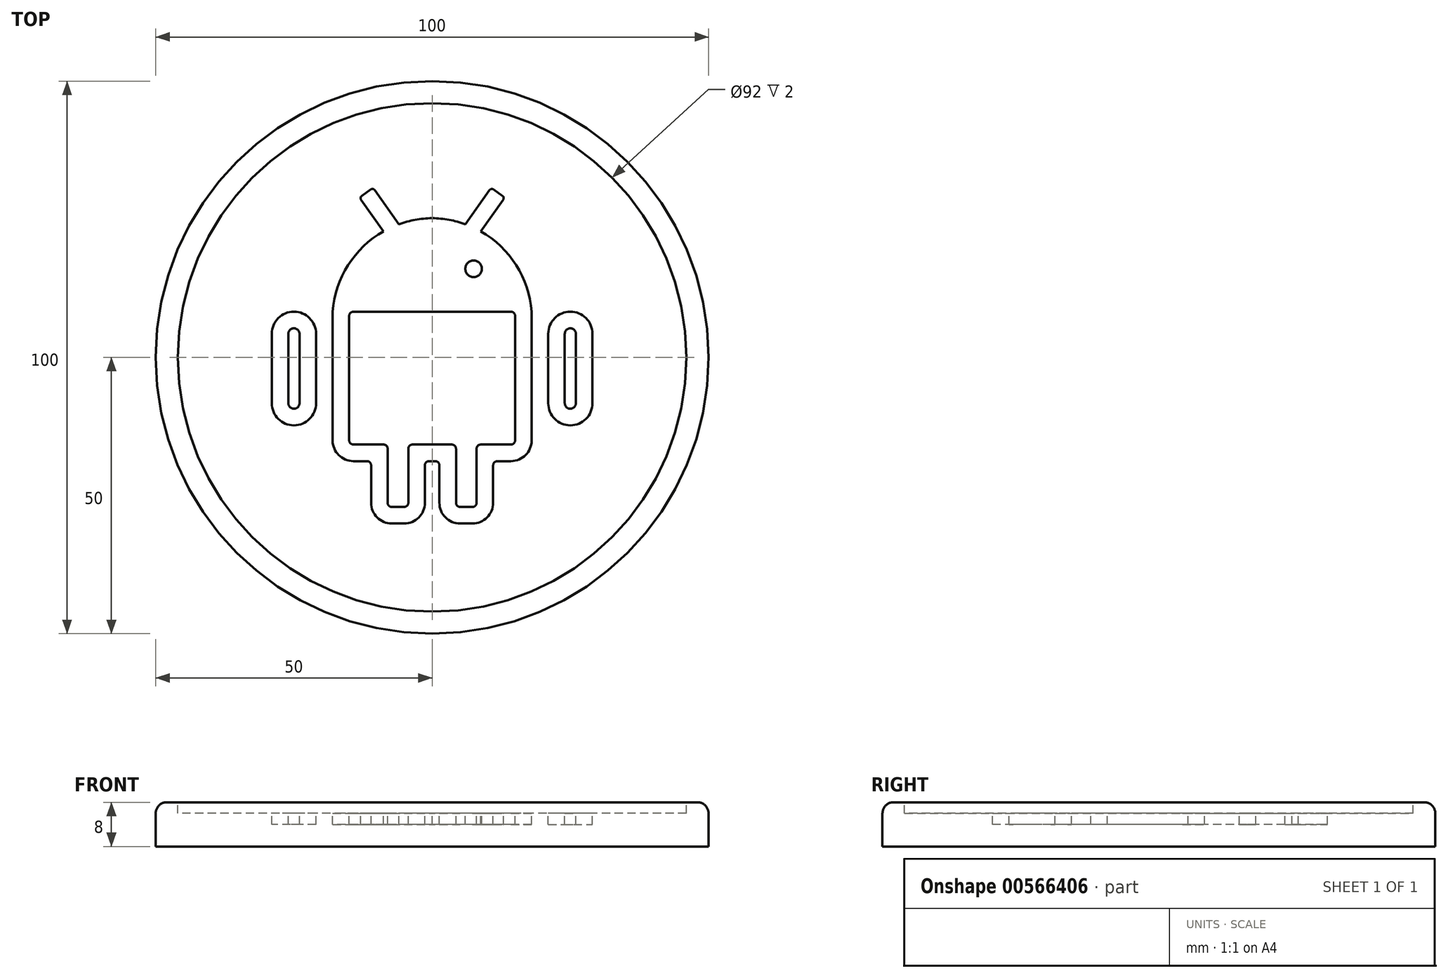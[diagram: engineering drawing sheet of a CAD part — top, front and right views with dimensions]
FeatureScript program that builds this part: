
annotation { "Feature Type Name" : "Feature", "Feature Type Description" : "" }
export const myFeature = defineFeature(function(context is Context, id is Id, definition is map)
    precondition{}
    {
        {
            var Q0;
            Q0=qCreatedBy(makeId("Top.planeOp"),FACE);
            var sketch = newSketch(context, id + "F0", { "sketchPlane" : qUnion([Q0])});
            skCircle(sketch, "E0", {"center": v(0, 0) * mm, "radius": 50 * mm});
            skSolve(sketch);
        }
        {
            assignVariable(context, id + "F1", {"name" : "Extrude", "anyValue" : 8 * mm});
        }
        {
            var Q0;
            Q0 = qSketchRegion(id + "F0", true);
            extrude(context, id + "F2", {"entities" : qUnion([Q0]), "depth" : getVariable(context, 'Extrude'), "offsetDistance" : 25 * mm});
        }
        {
            assignVariable(context, id + "F3", {"name" : "Fillet", "anyValue" : 2 * mm});
        }
        {
            var Q0;
            Q0=makeQuery(id+"F2.opExtrude","CAP_EDGE",EDGE,{"disambiguationData":[OSD([sQuery(id+"F0.wireOp",EDGE,"E0")])],"isStart":false});
            fillet(context, id + "F4", {"entities" : qUnion([Q0]), "radius" : getVariable(context, 'Fillet'), "tangentPropagation" : true, "allowEdgeOverflow" : false});
        }
        {
            assignVariable(context, id + "F5", {"name" : "Remove", "anyValue" : 2 * mm});
        }
        {
            var Q0;
            Q0=makeQuery(id+"F2.opExtrude","CAP_FACE",FACE,{"disambiguationData":[OSD([sQuery(id+"F0.wireOp",EDGE,"E0")])],"isStart":false});
            var sketch = newSketch(context, id + "F6", { "sketchPlane" : qUnion([Q0])});
            skCircle(sketch, "E1.0", {"center": v(0, 0) * mm, "radius": 48 * mm, "construction": true});
            skCircle(sketch, "E2", {"center": v(0, 0) * mm, "radius": 46 * mm});
            skSolve(sketch);
        }
        {
            var Q0;
            Q0 = qSketchRegion(id + "F6", true);
            extrude(context, id + "F7", {"entities" : qUnion([Q0]), "operationType" : NewBodyOperationType.REMOVE, "oppositeDirection" : true, "depth" : getVariable(context, 'Remove'), "offsetDistance" : 25 * mm});
        }
        {
            var Q0;
            Q0=makeQuery(id+"F7.boolean.opBoolean","COPY",FACE,{"derivedFrom":makeQuery(id+"F7.opExtrude","CAP_FACE",FACE,{"disambiguationData":[OSD([sQuery(id+"F6.wireOp",EDGE,"E2")])],"isStart":false})});
            var sketch = newSketch(context, id + "F8", { "sketchPlane" : qUnion([Q0])});
            skLineSegment(sketch, "E3", {"start": v(0, 48) * mm, "end": v(0, -48) * mm, "construction": true});
            skLineSegment(sketch, "E4", {"start": v(-26, 0) * mm, "end": v(48, 0) * mm, "construction": true});
            skLineSegment(sketch, "E5", {"start": v(-26, 30.77) * mm, "end": v(26, -30.77) * mm, "construction": true});
            skLineSegment(sketch, "E6", {"start": v(26, 30.77) * mm, "end": v(-26, -30.77) * mm, "construction": true});
            skPoint(sketch, "E7", {"position": v(0, 0) * mm});
            skLineSegment(sketch, "E8", {"start": v(0, 8.27) * mm, "end": v(-14.25, 8.27) * mm});
            skLineSegment(sketch, "E9", {"start": v(-15, 7.52) * mm, "end": v(-15, -15.02) * mm});
            skLineSegment(sketch, "E10", {"start": v(-14.25, -15.77) * mm, "end": v(-8.8, -15.77) * mm});
            skLineSegment(sketch, "E11", {"start": v(-8.04, -16.52) * mm, "end": v(-8.04, -26.32) * mm});
            skLineSegment(sketch, "E12", {"start": v(-7.3, -27.07) * mm, "end": v(-5.06, -27.07) * mm});
            skLineSegment(sketch, "E13", {"start": v(-4.31, -26.32) * mm, "end": v(-4.31, -16.52) * mm});
            skLineSegment(sketch, "E14", {"start": v(-3.56, -15.77) * mm, "end": v(0, -15.77) * mm});
            skLineSegment(sketch, "E15", {"start": v(0, 9.77) * mm, "end": v(-15, 9.77) * mm});
            skPoint(sketch, "E16.visualSharp", {"position": v(-15, 8.27) * mm});
            skArc(sketch, "E16.filletArc", {"start": v(-14.25, 8.27) * mm, "mid": v(-14.78, 8.05) * mm, "end": v(-15, 7.52) * mm});
            skPoint(sketch, "E17.visualSharp", {"position": v(-15, -15.77) * mm});
            skArc(sketch, "E17.filletArc", {"start": v(-15, -15.02) * mm, "mid": v(-14.78, -15.55) * mm, "end": v(-14.25, -15.77) * mm});
            skPoint(sketch, "E18.visualSharp", {"position": v(-8.04, -15.77) * mm});
            skArc(sketch, "E18.filletArc", {"start": v(-8.04, -16.52) * mm, "mid": v(-8.26, -16) * mm, "end": v(-8.8, -15.77) * mm});
            skPoint(sketch, "E19.visualSharp", {"position": v(-8.04, -27.07) * mm});
            skArc(sketch, "E19.filletArc", {"start": v(-8.04, -26.32) * mm, "mid": v(-7.82, -26.85) * mm, "end": v(-7.3, -27.07) * mm});
            skPoint(sketch, "E20.visualSharp", {"position": v(-4.31, -27.07) * mm});
            skArc(sketch, "E20.filletArc", {"start": v(-5.06, -27.07) * mm, "mid": v(-4.53, -26.85) * mm, "end": v(-4.31, -26.32) * mm});
            skArc(sketch, "E21", {"start": v(0, 22.2) * mm, "mid": v(-9.67, 18.6) * mm, "end": v(-15, 9.77) * mm});
            skPoint(sketch, "E22.visualSharp", {"position": v(-4.31, -15.77) * mm});
            skArc(sketch, "E22.filletArc", {"start": v(-3.56, -15.77) * mm, "mid": v(-4.1, -16) * mm, "end": v(-4.31, -16.52) * mm});
            skCircle(sketch, "E23", {"center": v(-7.5, 16.03) * mm, "radius": 1.5 * mm});
            skLineSegment(sketch, "E24", {"start": v(-6, 17.53) * mm, "end": v(-6, 16.37) * mm, "construction": true});
            skLineSegment(sketch, "E25", {"start": v(-6, 17.53) * mm, "end": v(-8.55, 17.53) * mm, "construction": true});
            skLineSegment(sketch, "E26.0", {"start": v(-0.56, -18.77) * mm, "end": v(0, -18.77) * mm});
            skLineSegment(sketch, "E26.1", {"start": v(-1.31, -26.32) * mm, "end": v(-1.31, -19.52) * mm});
            skLineSegment(sketch, "E26.2", {"start": v(-11.04, -19.52) * mm, "end": v(-11.04, -26.32) * mm});
            skArc(sketch, "E26.3", {"start": v(-11.04, -26.32) * mm, "mid": v(-9.94, -28.97) * mm, "end": v(-7.3, -30.07) * mm});
            skLineSegment(sketch, "E26.4", {"start": v(-7.3, -30.07) * mm, "end": v(-5.06, -30.07) * mm});
            skArc(sketch, "E26.5", {"start": v(-5.06, -30.07) * mm, "mid": v(-2.41, -28.97) * mm, "end": v(-1.31, -26.32) * mm});
            skLineSegment(sketch, "E27.0", {"start": v(-14.25, -18.77) * mm, "end": v(-11.8, -18.77) * mm});
            skLineSegment(sketch, "E27.3", {"start": v(-18, 8.27) * mm, "end": v(-18, -15.02) * mm});
            skArc(sketch, "E27.4", {"start": v(-18, -15.02) * mm, "mid": v(-16.9, -17.68) * mm, "end": v(-14.25, -18.77) * mm});
            skPoint(sketch, "E28.visualSharp", {"position": v(-11.04, -18.77) * mm});
            skArc(sketch, "E28.filletArc", {"start": v(-11.04, -19.52) * mm, "mid": v(-11.26, -19) * mm, "end": v(-11.8, -18.77) * mm});
            skArc(sketch, "E29", {"start": v(0, 25.2) * mm, "mid": v(-3.06, 24.89) * mm, "end": v(-6.02, 24.08) * mm});
            skLineSegment(sketch, "E30", {"start": v(-8.8, 22.8) * mm, "end": v(-12.85, 28.53) * mm});
            skLineSegment(sketch, "E31", {"start": v(-12.73, 29.23) * mm, "end": v(-11.1, 30.39) * mm});
            skLineSegment(sketch, "E32", {"start": v(-10.4, 30.27) * mm, "end": v(-6.02, 24.08) * mm});
            skPoint(sketch, "E33.visualSharp", {"position": v(-13.14, 28.94) * mm});
            skArc(sketch, "E33.filletArc", {"start": v(-12.73, 29.23) * mm, "mid": v(-12.93, 28.9) * mm, "end": v(-12.85, 28.53) * mm});
            skPoint(sketch, "E34.visualSharp", {"position": v(-10.69, 30.67) * mm});
            skArc(sketch, "E34.filletArc", {"start": v(-10.4, 30.27) * mm, "mid": v(-10.72, 30.47) * mm, "end": v(-11.1, 30.39) * mm});
            skArc(sketch, "E35", {"start": v(-8.8, 22.8) * mm, "mid": v(-15.2, 16.68) * mm, "end": v(-18, 8.27) * mm});
            skArc(sketch, "E36", {"start": v(-6.02, 24.08) * mm, "mid": v(-7.43, 23.5) * mm, "end": v(-8.8, 22.8) * mm, "construction": true});
            skLineSegment(sketch, "E37.left", {"start": v(-21, 4.27) * mm, "end": v(-21, -8.3) * mm});
            skLineSegment(sketch, "E37.right", {"start": v(-29, 4.27) * mm, "end": v(-29, -8.3) * mm});
            skPoint(sketch, "E38.orphan", {"position": v(-48, 0) * mm});
            skArc(sketch, "E39", {"start": v(-21, 4.27) * mm, "mid": v(-25, 8.27) * mm, "end": v(-29, 4.27) * mm});
            skArc(sketch, "E40", {"start": v(-29, -8.3) * mm, "mid": v(-25, -12.3) * mm, "end": v(-21, -8.3) * mm});
            skPoint(sketch, "E41", {"position": v(-25, 8.27) * mm});
            skLineSegment(sketch, "E42.0", {"start": v(-26, 4.27) * mm, "end": v(-26, -8.3) * mm});
            skArc(sketch, "E42.1", {"start": v(-24, 4.27) * mm, "mid": v(-25, 5.27) * mm, "end": v(-26, 4.27) * mm});
            skLineSegment(sketch, "E42.2", {"start": v(-24, 4.27) * mm, "end": v(-24, -8.3) * mm});
            skArc(sketch, "E42.3", {"start": v(-26, -8.3) * mm, "mid": v(-25, -9.3) * mm, "end": v(-24, -8.3) * mm});
            skArc(sketch, "E43.MirrorCS", {"start": v(8.8, 22.8) * mm, "mid": v(15.2, 16.68) * mm, "end": v(18, 8.27) * mm});
            skArc(sketch, "E44.MirrorCS", {"start": v(10.4, 30.27) * mm, "mid": v(10.72, 30.47) * mm, "end": v(11.1, 30.39) * mm});
            skArc(sketch, "E45.MirrorCS", {"start": v(12.73, 29.23) * mm, "mid": v(12.93, 28.9) * mm, "end": v(12.85, 28.53) * mm});
            skLineSegment(sketch, "E46.MirrorCS", {"start": v(12.73, 29.23) * mm, "end": v(11.1, 30.39) * mm});
            skLineSegment(sketch, "E47.MirrorCS", {"start": v(10.4, 30.27) * mm, "end": v(6.02, 24.08) * mm});
            skLineSegment(sketch, "E48.MirrorCS", {"start": v(8.8, 22.8) * mm, "end": v(12.85, 28.53) * mm});
            skArc(sketch, "E49.MirrorCS", {"start": v(0, 22.2) * mm, "mid": v(9.67, 18.6) * mm, "end": v(15, 9.77) * mm});
            skArc(sketch, "E50.MirrorCS", {"start": v(0, 25.2) * mm, "mid": v(3.06, 24.89) * mm, "end": v(6.02, 24.08) * mm});
            skArc(sketch, "E51.MirrorCS", {"start": v(14.25, 8.27) * mm, "mid": v(14.78, 8.05) * mm, "end": v(15, 7.52) * mm});
            skLineSegment(sketch, "E52.MirrorCS", {"start": v(0, 9.77) * mm, "end": v(15, 9.77) * mm});
            skLineSegment(sketch, "E53.MirrorCS", {"start": v(0, 8.27) * mm, "end": v(14.25, 8.27) * mm});
            skLineSegment(sketch, "E54.MirrorCS", {"start": v(15, 7.52) * mm, "end": v(15, -15.02) * mm});
            skLineSegment(sketch, "E55.MirrorCS", {"start": v(18, 8.27) * mm, "end": v(18, -15.02) * mm});
            skArc(sketch, "E56.MirrorCS", {"start": v(18, -15.02) * mm, "mid": v(16.9, -17.68) * mm, "end": v(14.25, -18.77) * mm});
            skArc(sketch, "E57.MirrorCS", {"start": v(15, -15.02) * mm, "mid": v(14.78, -15.55) * mm, "end": v(14.25, -15.77) * mm});
            skLineSegment(sketch, "E58.MirrorCS", {"start": v(14.25, -15.77) * mm, "end": v(8.8, -15.77) * mm});
            skLineSegment(sketch, "E59.MirrorCS", {"start": v(14.25, -18.77) * mm, "end": v(11.8, -18.77) * mm});
            skArc(sketch, "E60.MirrorCS", {"start": v(8.04, -16.52) * mm, "mid": v(8.26, -16) * mm, "end": v(8.8, -15.77) * mm});
            skArc(sketch, "E61.MirrorCS", {"start": v(11.04, -19.52) * mm, "mid": v(11.26, -19) * mm, "end": v(11.8, -18.77) * mm});
            skLineSegment(sketch, "E62.MirrorCS", {"start": v(11.04, -19.52) * mm, "end": v(11.04, -26.32) * mm});
            skLineSegment(sketch, "E63.MirrorCS", {"start": v(8.04, -16.52) * mm, "end": v(8.04, -26.32) * mm});
            skArc(sketch, "E64.MirrorCS", {"start": v(11.04, -26.32) * mm, "mid": v(9.94, -28.97) * mm, "end": v(7.3, -30.07) * mm});
            skArc(sketch, "E65.MirrorCS", {"start": v(8.04, -26.32) * mm, "mid": v(7.82, -26.85) * mm, "end": v(7.3, -27.07) * mm});
            skLineSegment(sketch, "E66.MirrorCS", {"start": v(7.3, -30.07) * mm, "end": v(5.06, -30.07) * mm});
            skLineSegment(sketch, "E67.MirrorCS", {"start": v(7.3, -27.07) * mm, "end": v(5.06, -27.07) * mm});
            skArc(sketch, "E68.MirrorCS", {"start": v(5.06, -30.07) * mm, "mid": v(2.41, -28.97) * mm, "end": v(1.31, -26.32) * mm});
            skArc(sketch, "E69.MirrorCS", {"start": v(5.06, -27.07) * mm, "mid": v(4.53, -26.85) * mm, "end": v(4.31, -26.32) * mm});
            skLineSegment(sketch, "E70.MirrorCS", {"start": v(4.31, -26.32) * mm, "end": v(4.31, -16.52) * mm});
            skLineSegment(sketch, "E71.MirrorCS", {"start": v(1.31, -26.32) * mm, "end": v(1.31, -19.52) * mm});
            skLineSegment(sketch, "E72.MirrorCS", {"start": v(3.56, -15.77) * mm, "end": v(0, -15.77) * mm});
            skArc(sketch, "E73.MirrorCS", {"start": v(3.56, -15.77) * mm, "mid": v(4.1, -16) * mm, "end": v(4.31, -16.52) * mm});
            skLineSegment(sketch, "E74.MirrorCS", {"start": v(0.56, -18.77) * mm, "end": v(0, -18.77) * mm});
            skArc(sketch, "E75.MirrorCS", {"start": v(29, -8.3) * mm, "mid": v(25, -12.3) * mm, "end": v(21, -8.3) * mm});
            skArc(sketch, "E76.MirrorCS", {"start": v(26, -8.3) * mm, "mid": v(25, -9.3) * mm, "end": v(24, -8.3) * mm});
            skLineSegment(sketch, "E77.MirrorCS", {"start": v(26, 4.27) * mm, "end": v(26, -8.3) * mm});
            skLineSegment(sketch, "E78.MirrorCS", {"start": v(29, 4.27) * mm, "end": v(29, -8.3) * mm});
            skLineSegment(sketch, "E79.MirrorCS", {"start": v(24, 4.27) * mm, "end": v(24, -8.3) * mm});
            skLineSegment(sketch, "E80.MirrorCS", {"start": v(21, 4.27) * mm, "end": v(21, -8.3) * mm});
            skArc(sketch, "E81.MirrorCS", {"start": v(24, 4.27) * mm, "mid": v(25, 5.27) * mm, "end": v(26, 4.27) * mm});
            skArc(sketch, "E82.MirrorCS", {"start": v(21, 4.27) * mm, "mid": v(25, 8.27) * mm, "end": v(29, 4.27) * mm});
            skPoint(sketch, "E83.visualSharp", {"position": v(-1.31, -18.77) * mm});
            skArc(sketch, "E83.filletArc", {"start": v(-0.56, -18.77) * mm, "mid": v(-1.1, -19) * mm, "end": v(-1.31, -19.52) * mm});
            skPoint(sketch, "E84.visualSharp", {"position": v(1.31, -18.77) * mm});
            skArc(sketch, "E84.filletArc", {"start": v(1.31, -19.52) * mm, "mid": v(1.1, -19) * mm, "end": v(0.56, -18.77) * mm});
            skCircle(sketch, "E85.MirrorC", {"center": v(7.5, 16.03) * mm, "radius": 1.5 * mm});
            skSolve(sketch);
        }
        {
            var Q0;
            Q0 = qSketchRegion(id + "F8", true);
            extrude(context, id + "F9", {"entities" : qUnion([Q0]), "operationType" : NewBodyOperationType.REMOVE, "oppositeDirection" : true, "depth" : getVariable(context, 'Remove'), "offsetDistance" : 25 * mm});
        }
        {
            var Q0;
            Q0=makeQuery(id+"F8.imprint","IMPRINT",FACE,{"disambiguationData":[TD([[makeQuery(id+"F8.imprint","IMPRINT",EDGE,{"derivedFrom":sQuery(id+"F8.wireOp",EDGE,"E23")}),1.0]])]});
            var Q1;
            Q1=makeQuery(id+"F8.imprint","IMPRINT",FACE,{"disambiguationData":[TD([[makeQuery(id+"F8.imprint","IMPRINT",EDGE,{"derivedFrom":sQuery(id+"F8.wireOp",EDGE,"E85.MirrorC")}),-1.0]])]});
            extrude(context, id + "F10", {"entities" : qUnion([Q0, Q1]), "operationType" : NewBodyOperationType.REMOVE, "oppositeDirection" : true, "depth" : getVariable(context, 'Remove'), "offsetDistance" : 25 * mm});
        }
    });
